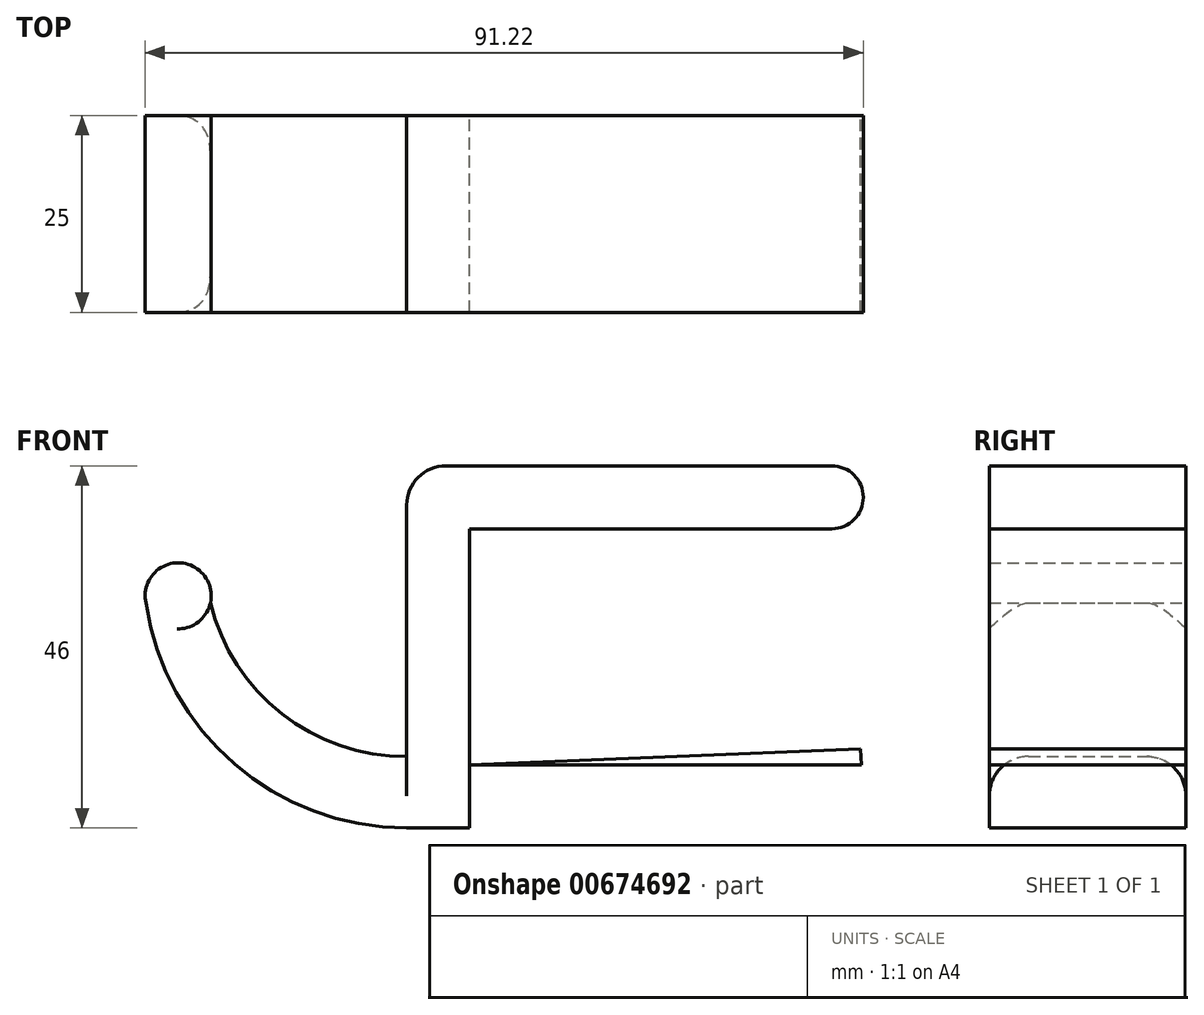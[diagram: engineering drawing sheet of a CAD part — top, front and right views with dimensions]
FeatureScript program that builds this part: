
annotation { "Feature Type Name" : "Feature", "Feature Type Description" : "" }
export const myFeature = defineFeature(function(context is Context, id is Id, definition is map)
    precondition{}
    {
        {
            var Q0;
            Q0=qCreatedBy(makeId("Front.planeOp"),FACE);
            var sketch = newSketch(context, id + "F0", { "sketchPlane" : qUnion([Q0])});
            skLineSegment(sketch, "E0.bottom", {"start": v(0, 0) * mm, "end": v(8, 0) * mm});
            skLineSegment(sketch, "E0.top", {"start": v(0, 46) * mm, "end": v(8, 46) * mm});
            skLineSegment(sketch, "E0.left", {"start": v(0, 0) * mm, "end": v(0, 46) * mm});
            skLineSegment(sketch, "E0.right", {"start": v(8, 0) * mm, "end": v(8, 46) * mm});
            skLineSegment(sketch, "E1.bottom", {"start": v(8, 46) * mm, "end": v(58, 46) * mm});
            skLineSegment(sketch, "E1.top", {"start": v(8, 38) * mm, "end": v(58, 38) * mm});
            skLineSegment(sketch, "E1.left", {"start": v(8, 46) * mm, "end": v(8, 38) * mm});
            skLineSegment(sketch, "E1.right", {"start": v(58, 46) * mm, "end": v(58, 38) * mm});
            skLineSegment(sketch, "E2.bottom", {"start": v(8, 0) * mm, "end": v(58, 0) * mm});
            skLineSegment(sketch, "E2.top", {"start": v(8, 8) * mm, "end": v(58, 8) * mm});
            skLineSegment(sketch, "E2.left", {"start": v(8, 0) * mm, "end": v(8, 8) * mm});
            skLineSegment(sketch, "E2.right", {"start": v(58, 0) * mm, "end": v(58, 8) * mm});
            skArc(sketch, "E3", {"start": v(-33.12, 28.59) * mm, "mid": v(-21.88, 8.14) * mm, "end": v(0, 0) * mm});
            skArc(sketch, "E4", {"start": v(-24.92, 28.59) * mm, "mid": v(-15.85, 14.5) * mm, "end": v(0, 9.08) * mm});
            skArc(sketch, "E5", {"start": v(-24.92, 28.59) * mm, "mid": v(-29.02, 33.68) * mm, "end": v(-33.12, 28.59) * mm});
            skLineSegment(sketch, "E6", {"start": v(8, 8) * mm, "end": v(57.66, 10.04) * mm});
            skLineSegment(sketch, "E7", {"start": v(57.66, 10.04) * mm, "end": v(58, 1.77) * mm});
            skPoint(sketch, "E7.endSnap0", {"position": v(58, 4) * mm});
            skLineSegment(sketch, "E8", {"start": v(58, 1.77) * mm, "end": v(8, 0) * mm});
            skSolve(sketch);
        }
        {
            var Q0;
            {var subQ0=sQuery(id+"F0.wireOp",EDGE,"E3");Q0=makeQuery(id+"F0.imprint","IMPRINT",FACE,{"disambiguationData":[TD([[makeQuery(id+"F0.imprint","IMPRINT",EDGE,{"derivedFrom":subQ0}),1.0]])]});}
            var Q1;
            Q1=makeQuery(id+"F0.imprint","IMPRINT",FACE,{"disambiguationData":[TD([[makeQuery(id+"F0.imprint","IMPRINT",EDGE,{"derivedFrom":sQuery(id+"F0.wireOp",EDGE,"E1.bottom")}),-1.0]])]});
            var Q2;
            {var subQ0=sQuery(id+"F0.wireOp",EDGE,"E6");Q2=makeQuery(id+"F0.imprint","IMPRINT",FACE,{"disambiguationData":[TD([[makeQuery(id+"F0.imprint","IMPRINT",EDGE,{"derivedFrom":subQ0}),-1.0]])]});}
            var Q3;
            {var subQ3=sQuery(id+"F0.wireOp",EDGE,"E0.bottom");Q3=makeQuery(id+"F0.imprint","IMPRINT",FACE,{"disambiguationData":[TD([[makeQuery(id+"F0.imprint","IMPRINT",EDGE,{"derivedFrom":subQ3}),1.0]])]});}
            var Q4;
            {var subQ0=sQuery(id+"F0.wireOp",EDGE,"E2.left");Q4=makeQuery(id+"F0.imprint","IMPRINT",FACE,{"disambiguationData":[TD([[makeQuery(id+"F0.imprint","IMPRINT",EDGE,{"derivedFrom":subQ0}),-1.0]])]});}
            extrude(context, id + "F1", {"entities" : qUnion([Q0, Q1, Q2, Q3, Q4]), "depth" : 25 * mm, "offsetDistance" : 25 * mm});
        }
        {
            var Q0;
            Q0=makeQuery(id+"F1.opExtrude","SWEPT_EDGE",EDGE,{"disambiguationData":[OSD([sQuery(id+"F0.wireOp",EDGE,"E1.bottom"),sQuery(id+"F0.wireOp",EDGE,"E1.right")])]});
            var Q1;
            Q1=makeQuery(id+"F1.opExtrude","SWEPT_EDGE",EDGE,{"disambiguationData":[OSD([sQuery(id+"F0.wireOp",EDGE,"E1.top"),sQuery(id+"F0.wireOp",EDGE,"E1.right")])]});
            var Q2;
            Q2=makeQuery(id+"F1.opExtrude","SWEPT_EDGE",EDGE,{"disambiguationData":[OSD([sQuery(id+"F0.wireOp",EDGE,"E6"),sQuery(id+"F0.wireOp",EDGE,"E7")])]});
            var Q3;
            Q3=makeQuery(id+"F1.opExtrude","SWEPT_EDGE",EDGE,{"disambiguationData":[OSD([sQuery(id+"F0.wireOp",EDGE,"E2.right"),sQuery(id+"F0.wireOp",EDGE,"E7"),sQuery(id+"F0.wireOp",EDGE,"E8")])]});
            fillet(context, id + "F2", {"entities" : qUnion([Q0, Q1, Q2, Q3]), "radius" : 4 * mm, "tangentPropagation" : true, "allowEdgeOverflow" : false});
        }
        {
            var Q0;
            Q0=makeQuery(id+"F1.opExtrude","CAP_EDGE",EDGE,{"disambiguationData":[OSD([sQuery(id+"F0.wireOp",EDGE,"E4")])],"isStart":false});
            var Q1;
            Q1=makeQuery(id+"F1.opExtrude","CAP_EDGE",EDGE,{"disambiguationData":[OSD([sQuery(id+"F0.wireOp",EDGE,"E4")])],"isStart":true});
            var Q2;
            Q2=makeQuery(id+"F1.opExtrude","SWEPT_EDGE",EDGE,{"disambiguationData":[OSD([sQuery(id+"F0.wireOp",EDGE,"E0.top"),sQuery(id+"F0.wireOp",EDGE,"E0.left")])]});
            fillet(context, id + "F3", {"entities" : qUnion([Q0, Q1, Q2]), "radius" : 5 * mm, "tangentPropagation" : true, "allowEdgeOverflow" : false});
        }
    });
